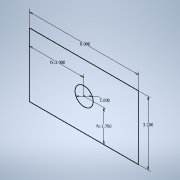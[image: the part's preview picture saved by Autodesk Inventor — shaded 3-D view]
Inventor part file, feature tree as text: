
AUTODESK INVENTOR PART (.ipt)
format: ipt  version: 2020 (Build 240168000, 168)  size: 92,160 bytes
history: native  units: in
note: dims shown in document units (in); Inventor stores cm internally (conversion verified against a paired STEP export)
features: sketch x1
ambient origin geometry x8: Origin, YZ Plane, XZ Plane, XY Plane, X Axis, Y Axis, Z Axis, Center Point
feature tree (1):
  sketch  "Sketch1"  dims[d3=3.0in d4=1.75in]
